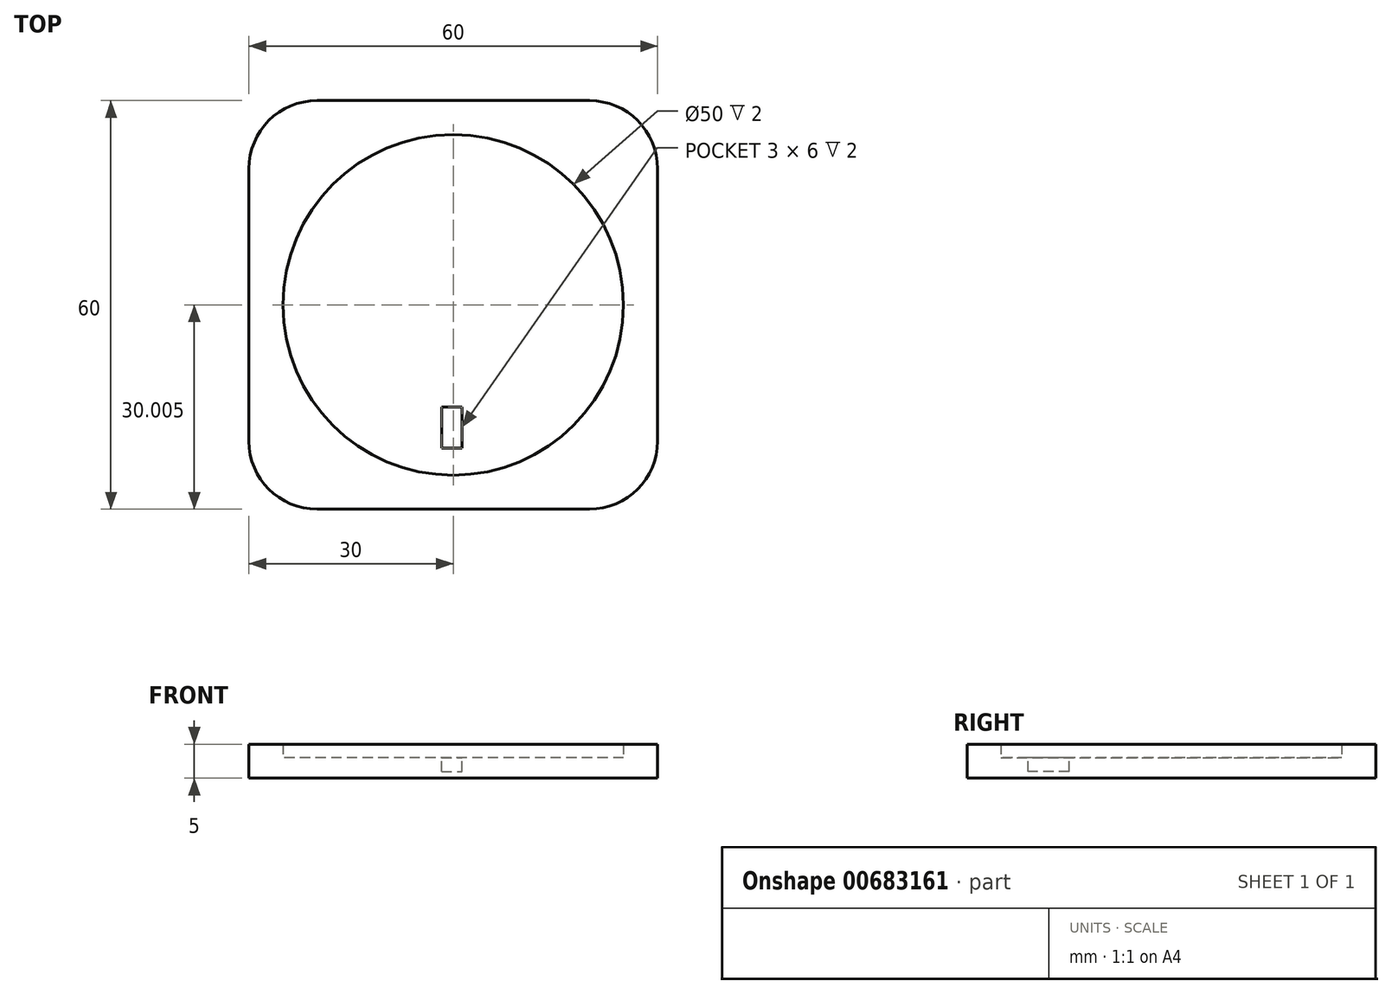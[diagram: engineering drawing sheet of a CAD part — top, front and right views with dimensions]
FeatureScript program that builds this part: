
annotation { "Feature Type Name" : "Feature", "Feature Type Description" : "" }
export const myFeature = defineFeature(function(context is Context, id is Id, definition is map)
    precondition{}
    {
        {
            var Q0;
            Q0=qCreatedBy(makeId("Top.planeOp"),FACE);
            var sketch = newSketch(context, id + "F0", { "sketchPlane" : qUnion([Q0])});
            skLineSegment(sketch, "E0.bottom", {"start": v(-20.3, 52.45) * mm, "end": v(-80.3, 52.45) * mm});
            skLineSegment(sketch, "E0.top", {"start": v(-20.3, -7.55) * mm, "end": v(-80.3, -7.55) * mm});
            skLineSegment(sketch, "E0.left", {"start": v(-20.3, 52.45) * mm, "end": v(-20.3, -7.55) * mm});
            skLineSegment(sketch, "E0.right", {"start": v(-80.3, 52.45) * mm, "end": v(-80.3, -7.55) * mm});
            skPoint(sketch, "E1", {"position": v(-50.3, 22.45) * mm});
            skPoint(sketch, "E1.positionSnap0", {"position": v(-50.3, -7.55) * mm});
            skPoint(sketch, "E1.positionSnap1", {"position": v(-20.3, 22.45) * mm});
            skCircle(sketch, "E2", {"center": v(-50.3, 22.45) * mm, "radius": 25 * mm});
            skSolve(sketch);
        }
        {
            var Q0;
            Q0=makeQuery(id+"F0.imprint","IMPRINT",FACE,{"disambiguationData":[TD([[makeQuery(id+"F0.imprint","IMPRINT",EDGE,{"derivedFrom":sQuery(id+"F0.wireOp",EDGE,"E0.bottom")}),1.0]])]});
            extrude(context, id + "F1", {"entities" : qUnion([Q0]), "depth" : 5 * mm, "offsetDistance" : 25 * mm});
        }
        {
            var Q0;
            Q0=makeQuery(id+"F0.imprint","IMPRINT",FACE,{"disambiguationData":[TD([[makeQuery(id+"F0.imprint","IMPRINT",EDGE,{"derivedFrom":sQuery(id+"F0.wireOp",EDGE,"E2")}),1.0]])]});
            extrude(context, id + "F2", {"entities" : qUnion([Q0]), "operationType" : NewBodyOperationType.ADD, "depth" : 3 * mm, "offsetDistance" : 25 * mm});
        }
        {
            var Q0;
            Q0=makeQuery(id+"F1.opExtrude","SWEPT_EDGE",EDGE,{"disambiguationData":[OSD([sQuery(id+"F0.wireOp",EDGE,"E0.top"),sQuery(id+"F0.wireOp",EDGE,"E0.left")])]});
            var Q1;
            Q1=makeQuery(id+"F1.opExtrude","SWEPT_EDGE",EDGE,{"disambiguationData":[OSD([sQuery(id+"F0.wireOp",EDGE,"E0.top"),sQuery(id+"F0.wireOp",EDGE,"E0.right")])]});
            var Q2;
            Q2=makeQuery(id+"F1.opExtrude","SWEPT_EDGE",EDGE,{"disambiguationData":[OSD([sQuery(id+"F0.wireOp",EDGE,"E0.bottom"),sQuery(id+"F0.wireOp",EDGE,"E0.right")])]});
            var Q3;
            Q3=makeQuery(id+"F1.opExtrude","SWEPT_EDGE",EDGE,{"disambiguationData":[OSD([sQuery(id+"F0.wireOp",EDGE,"E0.bottom"),sQuery(id+"F0.wireOp",EDGE,"E0.left")])]});
            fillet(context, id + "F3", {"entities" : qUnion([Q0, Q1, Q2, Q3]), "radius" : 10 * mm, "tangentPropagation" : true, "allowEdgeOverflow" : false});
        }
        {
            var Q0;
            Q0=makeQuery(id+"F2.opExtrude","CAP_FACE",FACE,{"disambiguationData":[OSD([sQuery(id+"F0.wireOp",EDGE,"E2")])],"isStart":false});
            var sketch = newSketch(context, id + "F4", { "sketchPlane" : qUnion([Q0])});
            skLineSegment(sketch, "E3.bottom", {"start": v(-52.02, 7.45) * mm, "end": v(-49.02, 7.45) * mm});
            skLineSegment(sketch, "E3.top", {"start": v(-52.02, 1.45) * mm, "end": v(-49.02, 1.45) * mm});
            skLineSegment(sketch, "E3.left", {"start": v(-52.02, 7.45) * mm, "end": v(-52.02, 1.45) * mm});
            skLineSegment(sketch, "E3.right", {"start": v(-49.02, 7.45) * mm, "end": v(-49.02, 1.45) * mm});
            skPoint(sketch, "E3.middle", {"position": v(-50.52, 4.45) * mm});
            skLineSegment(sketch, "E4.left", {"start": v(-52.02, 1.45) * mm, "end": v(-52.02, 7.45) * mm});
            skLineSegment(sketch, "E4.right", {"start": v(-49.02, 1.45) * mm, "end": v(-49.02, 7.45) * mm});
            skSolve(sketch);
        }
        {
            var Q0;
            Q0=makeQuery(id+"F4.imprint","IMPRINT",FACE,{"disambiguationData":[TD([[makeQuery(id+"F4.imprint","IMPRINT",EDGE,{"derivedFrom":sQuery(id+"F4.wireOp",EDGE,"E3.top")}),1.0]])]});
            extrude(context, id + "F5", {"entities" : qUnion([Q0]), "operationType" : NewBodyOperationType.REMOVE, "oppositeDirection" : true, "depth" : 2 * mm, "offsetDistance" : 25 * mm});
        }
    });
